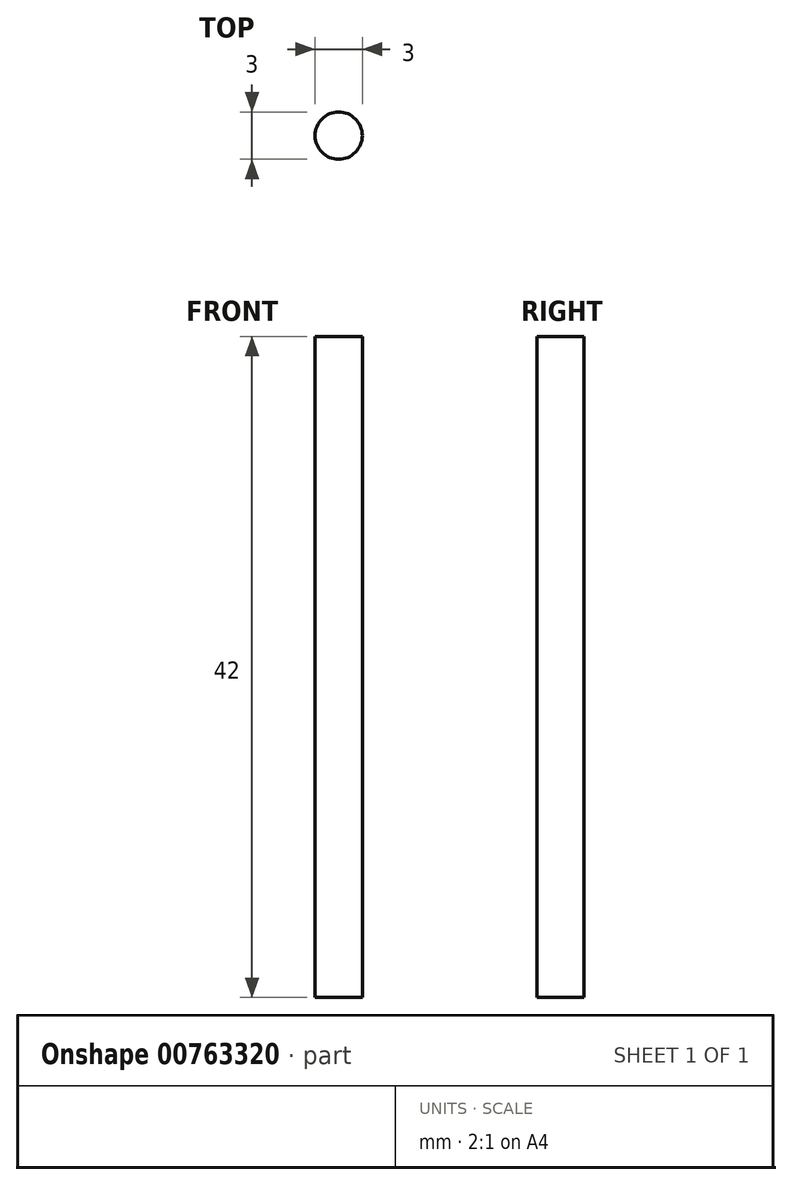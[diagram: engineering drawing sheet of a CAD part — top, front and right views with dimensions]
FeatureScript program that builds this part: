
annotation { "Feature Type Name" : "Feature", "Feature Type Description" : "" }
export const myFeature = defineFeature(function(context is Context, id is Id, definition is map)
    precondition{}
    {
        {
            var Q0;
            Q0=qCreatedBy(makeId("Top.planeOp"),FACE);
            var sketch = newSketch(context, id + "F0", { "sketchPlane" : qUnion([Q0])});
            skCircle(sketch, "E0", {"center": v(0, 0) * mm, "radius": 1.5 * mm});
            skSolve(sketch);
        }
        {
            var Q0;
            Q0=makeQuery(id+"F0.imprint","IMPRINT",FACE,{"disambiguationData":[TD([[makeQuery(id+"F0.imprint","IMPRINT",EDGE,{"derivedFrom":sQuery(id+"F0.wireOp",EDGE,"E0")}),1.0]])]});
            extrude(context, id + "F1", {"entities" : qUnion([Q0]), "depth" : 42 * mm, "offsetDistance" : 25 * mm});
        }
    });
